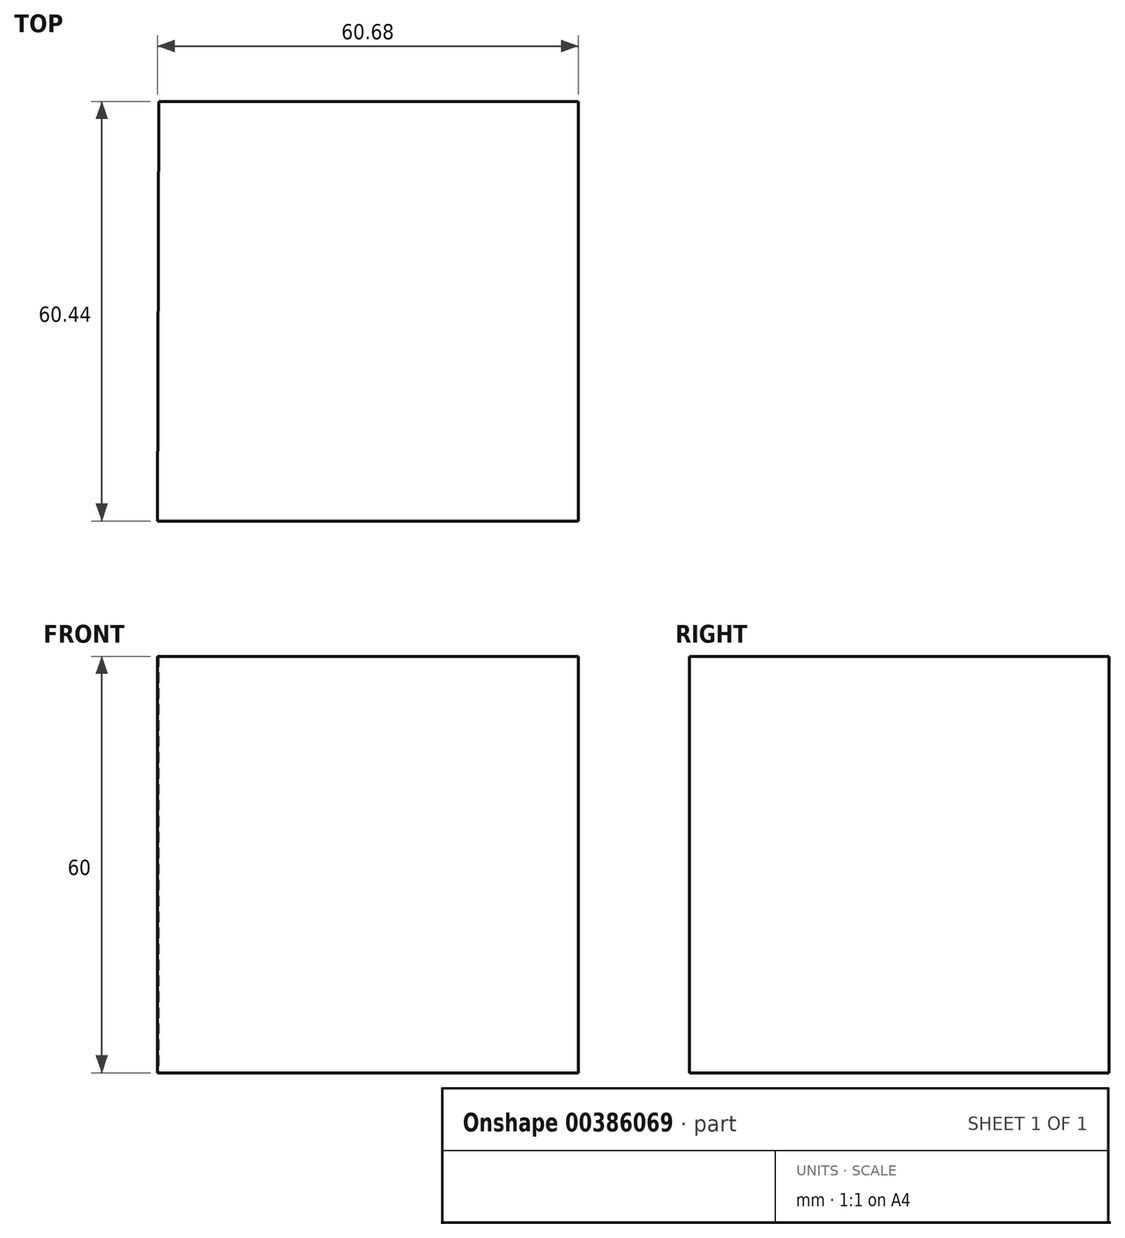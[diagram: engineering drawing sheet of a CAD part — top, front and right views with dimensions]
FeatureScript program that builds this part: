
annotation { "Feature Type Name" : "Feature", "Feature Type Description" : "" }
export const myFeature = defineFeature(function(context is Context, id is Id, definition is map)
    precondition{}
    {
        {
            var Q0;
            Q0=qCreatedBy(makeId("Top.planeOp"),FACE);
            var sketch = newSketch(context, id + "F0", { "sketchPlane" : qUnion([Q0])});
            skLineSegment(sketch, "E0", {"start": v(-35.7, 28.9) * mm, "end": v(24.8, 28.9) * mm});
            skLineSegment(sketch, "E1", {"start": v(24.8, 28.9) * mm, "end": v(24.8, -31.53) * mm});
            skLineSegment(sketch, "E2", {"start": v(24.8, -31.53) * mm, "end": v(-35.88, -31.53) * mm});
            skLineSegment(sketch, "E3", {"start": v(-35.88, -31.53) * mm, "end": v(-35.7, 28.9) * mm});
            skSolve(sketch);
        }
        {
            var Q0;
            Q0=makeQuery(id+"F0.imprint","IMPRINT",FACE,{"disambiguationData":[TD([[makeQuery(id+"F0.imprint","IMPRINT",EDGE,{"derivedFrom":sQuery(id+"F0.wireOp",EDGE,"E0")}),-1.0]])]});
            extrude(context, id + "F1", {"entities" : qUnion([Q0]), "depth" : 60 * mm});
        }
    });
